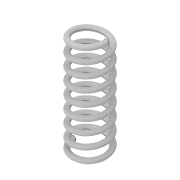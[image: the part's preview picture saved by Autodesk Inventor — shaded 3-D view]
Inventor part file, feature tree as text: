
AUTODESK INVENTOR PART (.ipt)
format: ipt  version: 2017 (Build 210142000, 142)  size: 562,688 bytes
history: native  units: in
note: dims shown in document units (in); Inventor stores cm internally (conversion verified against a paired STEP export)
features: helix x1, sketch x1
ambient origin geometry x8: Origin, YZ Plane, XZ Plane, XY Plane, X Axis, Y Axis, Z Axis, Center Point
bodies: Solid1 (feature_tree)
feature tree (2):
  helix  "Coil1"  [1 undecoded]
  sketch  "Sketch1"  dims[d1=1.575in d2=0.59in d3=1.0in d4=3.1496in d5=0.0in d6=90.0deg d7=90.0deg d8=0.0in d9=0.0in]
note: 1 required parameter value undecoded (feature->parameter linkage not recoverable at this tier; creation-order binding heuristic only, values carry confidence <= 0.55)
